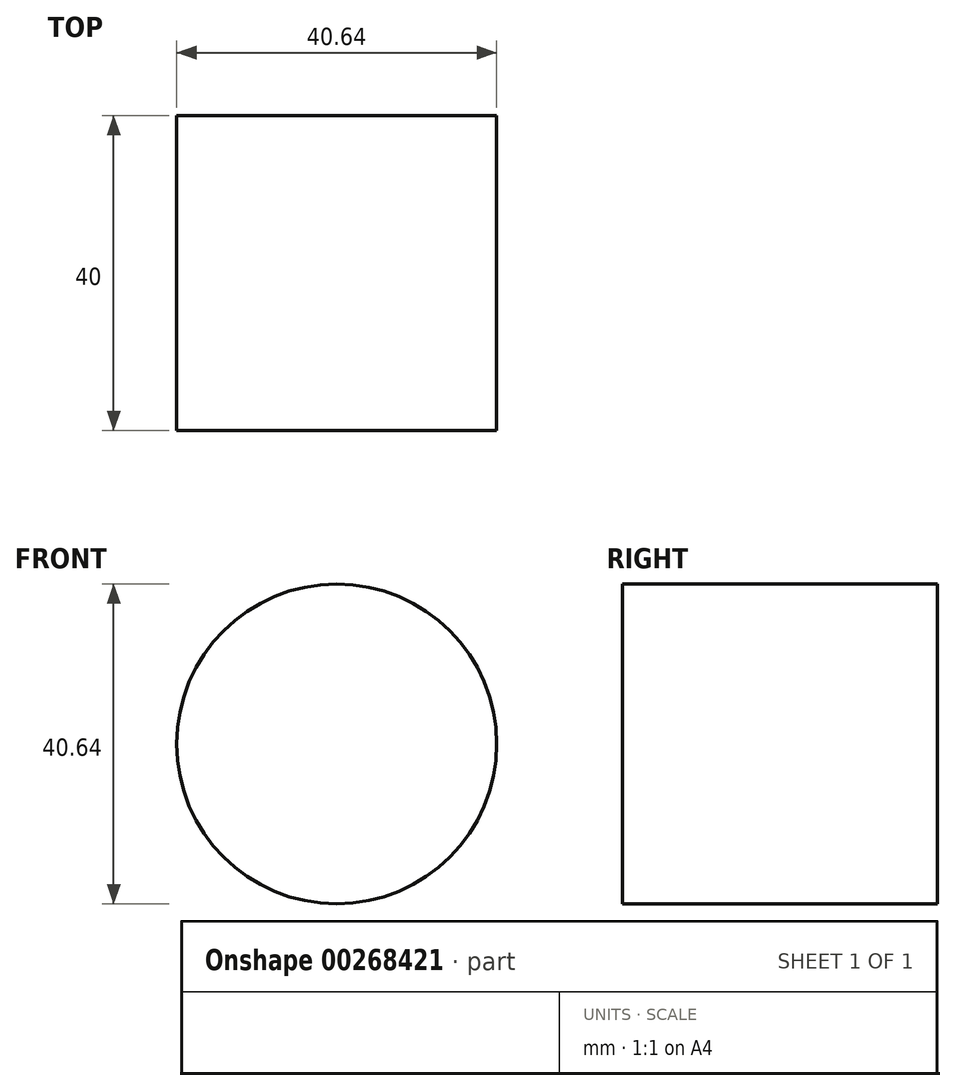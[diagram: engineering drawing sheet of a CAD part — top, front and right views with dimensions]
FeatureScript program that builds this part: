
annotation { "Feature Type Name" : "Feature", "Feature Type Description" : "" }
export const myFeature = defineFeature(function(context is Context, id is Id, definition is map)
    precondition{}
    {
        {
            var Q0;
            Q0=qCreatedBy(makeId("Front.planeOp"),FACE);
            var sketch = newSketch(context, id + "F0", { "sketchPlane" : qUnion([Q0])});
            skCircle(sketch, "E0", {"center": v(0, 0) * mm, "radius": 20.32 * mm});
            skSolve(sketch);
        }
        {
            var Q0;
            Q0=makeQuery(id+"F0.imprint","IMPRINT",FACE,{"disambiguationData":[TD([[makeQuery(id+"F0.imprint","IMPRINT",EDGE,{"derivedFrom":sQuery(id+"F0.wireOp",EDGE,"E0")}),1.0]])]});
            extrude(context, id + "F1", {"entities" : qUnion([Q0]), "depth" : 40 * mm});
        }
    });
